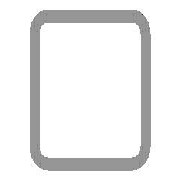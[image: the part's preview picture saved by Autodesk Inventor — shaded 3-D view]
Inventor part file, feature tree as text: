
AUTODESK INVENTOR PART (.ipt)
format: ipt  version: 2018 (Build 220112000, 112)  size: 129,536 bytes
history: native  units: mm (DEFAULTED — no unit token found)
features: other x4, sketch x3, extrude x1, plane x1
ambient origin geometry x8: Origin, YZ Plane, XZ Plane, XY Plane, X Axis, Y Axis, Z Axis, Center Point
bodies: Solid1 (feature_tree)
feature tree (9):
  other  "Tubolari horizontal"
  other  "Driven Length"
  other  "Piano iniziale"
  other  "Piano finale"
  extrude  "Corpo"  TaperAngle=0.0deg  [1 undecoded]
  sketch  "Schizzo"
  sketch  "Sketch3"  dims[d3=620.0mm d4=0.0mm]
  plane  "Work Plane3"
  sketch  "Sketch4"  dims[d7=4.0mm d9=40.0mm d11=40.0mm d12=2.0mm d13=-0.0mm d14=620.0mm d15=20.0mm d16=20.0mm d17=90.0deg d18=620.0mm]
note: 1 required parameter value undecoded (feature->parameter linkage not recoverable at this tier; creation-order binding heuristic only, values carry confidence <= 0.55)
